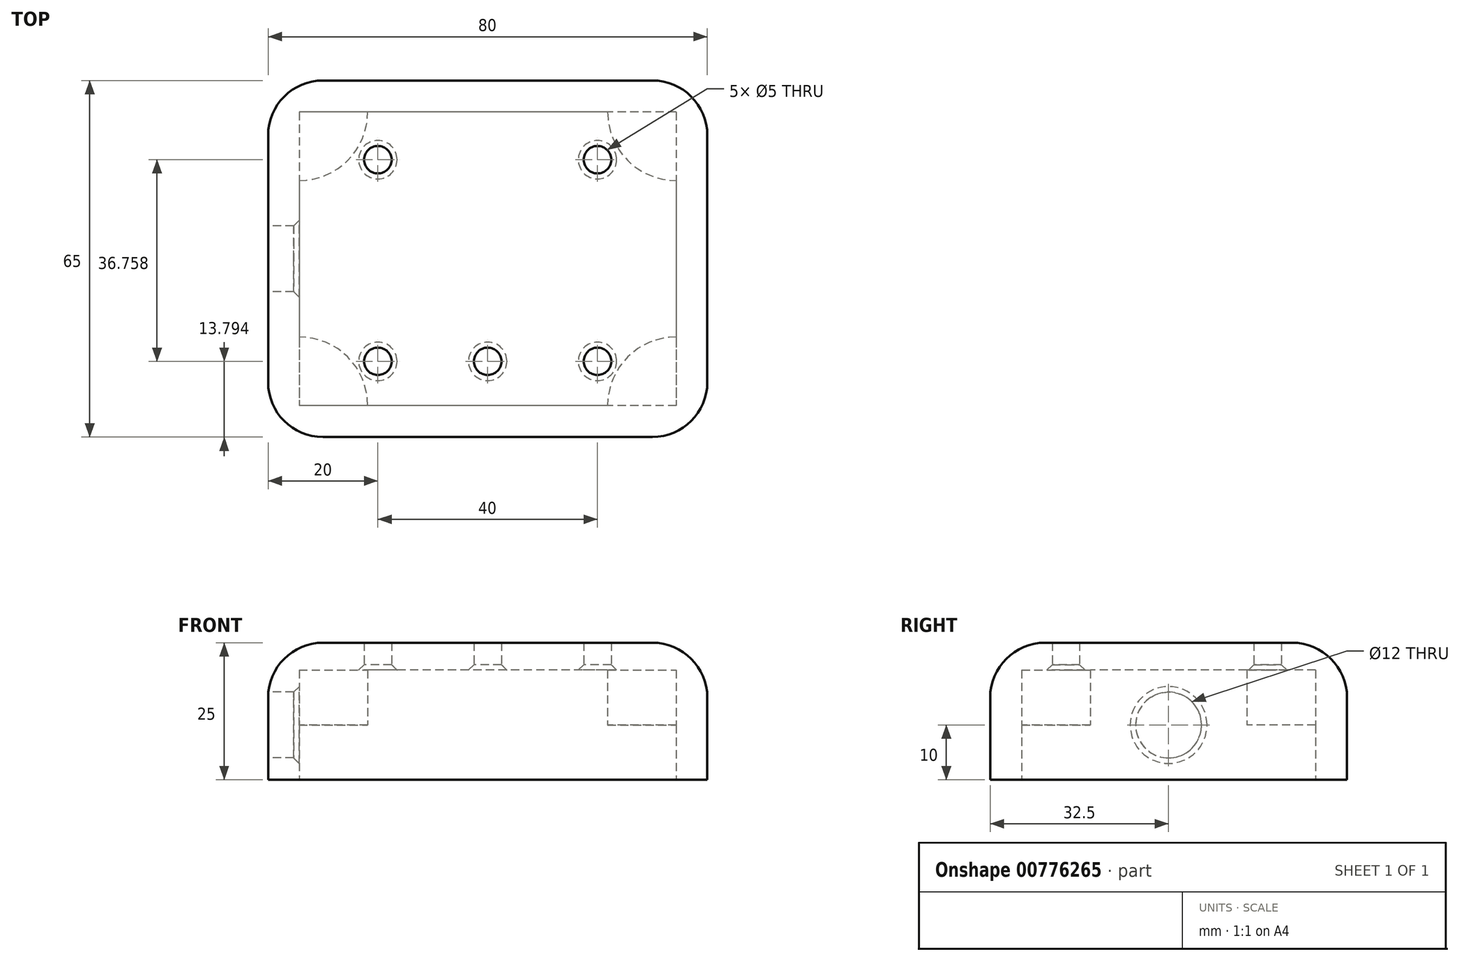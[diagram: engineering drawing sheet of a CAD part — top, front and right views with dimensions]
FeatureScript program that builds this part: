
annotation { "Feature Type Name" : "Feature", "Feature Type Description" : "" }
export const myFeature = defineFeature(function(context is Context, id is Id, definition is map)
    precondition{}
    {
        {
            var Q0;
            Q0=qCreatedBy(makeId("Top.planeOp"),FACE);
            var sketch = newSketch(context, id + "F0", { "sketchPlane" : qUnion([Q0])});
            skLineSegment(sketch, "E0.bottom", {"start": v(40, 32.5) * mm, "end": v(-40, 32.5) * mm});
            skLineSegment(sketch, "E0.top", {"start": v(40, -32.5) * mm, "end": v(-40, -32.5) * mm});
            skLineSegment(sketch, "E0.left", {"start": v(40, 32.5) * mm, "end": v(40, -32.5) * mm});
            skLineSegment(sketch, "E0.right", {"start": v(-40, 32.5) * mm, "end": v(-40, -32.5) * mm});
            skPoint(sketch, "E0.middle", {"position": v(0, 0) * mm});
            skCircle(sketch, "E1", {"center": v(-20, 18.05) * mm, "radius": 2.5 * mm});
            skCircle(sketch, "E2", {"center": v(20, 18.05) * mm, "radius": 2.5 * mm});
            skCircle(sketch, "E3", {"center": v(-20, -18.7) * mm, "radius": 2.5 * mm});
            skCircle(sketch, "E4", {"center": v(0, -18.7) * mm, "radius": 2.5 * mm});
            skCircle(sketch, "E5", {"center": v(20, -18.7) * mm, "radius": 2.5 * mm});
            skSolve(sketch);
        }
        {
            var Q0;
            Q0=qCreatedBy(makeId("Top.planeOp"),FACE);
            var sketch = newSketch(context, id + "F1", { "sketchPlane" : qUnion([Q0])});
            skLineSegment(sketch, "E6.bottom", {"start": v(34.35, 26.75) * mm, "end": v(-34.35, 26.75) * mm});
            skLineSegment(sketch, "E6.top", {"start": v(34.35, -26.75) * mm, "end": v(-34.35, -26.75) * mm});
            skLineSegment(sketch, "E6.left", {"start": v(34.35, 26.75) * mm, "end": v(34.35, -26.75) * mm});
            skLineSegment(sketch, "E6.right", {"start": v(-34.35, 26.75) * mm, "end": v(-34.35, -26.75) * mm});
            skPoint(sketch, "E6.middle", {"position": v(0, 0) * mm});
            skCircle(sketch, "E7", {"center": v(-34.35, 26.75) * mm, "radius": 12.5 * mm});
            skCircle(sketch, "E8", {"center": v(34.35, 26.75) * mm, "radius": 12.5 * mm});
            skCircle(sketch, "E9", {"center": v(34.35, -26.75) * mm, "radius": 12.5 * mm});
            skCircle(sketch, "E10", {"center": v(-34.35, -26.75) * mm, "radius": 12.5 * mm});
            skSolve(sketch);
        }
        {
            var Q0;
            Q0=makeQuery(id+"F0.imprint","IMPRINT",FACE,{"disambiguationData":[TD([[makeQuery(id+"F0.imprint","IMPRINT",EDGE,{"derivedFrom":sQuery(id+"F0.wireOp",EDGE,"E0.bottom")}),1.0]])]});
            extrude(context, id + "F2", {"entities" : qUnion([Q0]), "depth" : 25 * mm, "offsetDistance" : 25 * mm});
        }
        {
            var Q0;
            {var subQ5=sQuery(id+"F1.wireOp",EDGE,"E8");var subQ13=sQuery(id+"F1.wireOp",EDGE,"E6.bottom");var subQ14=makeQuery(id+"F1.imprint","INTERSECT",VERTEX,{"derivedFrom":[subQ13,subQ5]});Q0=makeQuery(id+"F1.imprint","IMPRINT",FACE,{"disambiguationData":[TD([[makeQuery(id+"F1.imprint","IMPRINT",EDGE,{"disambiguationData":[TD([[subQ14,-1.0]])],"derivedFrom":subQ13}),1.0]])]});}
            extrude(context, id + "F3", {"entities" : qUnion([Q0]), "operationType" : NewBodyOperationType.REMOVE, "depth" : 20 * mm, "offsetDistance" : 25 * mm});
        }
        {
            var Q0;
            {var subQ5=sQuery(id+"F1.wireOp",EDGE,"E8");var subQ13=sQuery(id+"F1.wireOp",EDGE,"E6.bottom");var subQ14=makeQuery(id+"F1.imprint","INTERSECT",VERTEX,{"derivedFrom":[subQ13,subQ5]});Q0=makeQuery(id+"F1.imprint","IMPRINT",FACE,{"disambiguationData":[TD([[makeQuery(id+"F1.imprint","IMPRINT",EDGE,{"disambiguationData":[TD([[subQ14,-1.0]])],"derivedFrom":subQ13}),1.0]])]});}
            var Q1;
            {var subQ0=sQuery(id+"F1.wireOp",EDGE,"E6.right");var subQ1=sQuery(id+"F1.wireOp",EDGE,"E6.bottom");var subQ2=makeQuery(id+"F1.imprint","INTERSECT",VERTEX,{"derivedFrom":[subQ1,subQ0]});Q1=makeQuery(id+"F1.imprint","IMPRINT",FACE,{"disambiguationData":[TD([[makeQuery(id+"F1.imprint","IMPRINT",EDGE,{"disambiguationData":[TD([[subQ2,1.0]])],"derivedFrom":subQ1}),1.0]])]});}
            var Q2;
            {var subQ0=sQuery(id+"F1.wireOp",EDGE,"E6.right");var subQ1=sQuery(id+"F1.wireOp",EDGE,"E6.top");var subQ2=makeQuery(id+"F1.imprint","INTERSECT",VERTEX,{"derivedFrom":[subQ1,subQ0]});Q2=makeQuery(id+"F1.imprint","IMPRINT",FACE,{"disambiguationData":[TD([[makeQuery(id+"F1.imprint","IMPRINT",EDGE,{"disambiguationData":[TD([[subQ2,1.0]])],"derivedFrom":subQ1}),-1.0]])]});}
            var Q3;
            {var subQ0=sQuery(id+"F1.wireOp",EDGE,"E6.left");var subQ1=sQuery(id+"F1.wireOp",EDGE,"E6.top");var subQ2=makeQuery(id+"F1.imprint","INTERSECT",VERTEX,{"derivedFrom":[subQ1,subQ0]});Q3=makeQuery(id+"F1.imprint","IMPRINT",FACE,{"disambiguationData":[TD([[makeQuery(id+"F1.imprint","IMPRINT",EDGE,{"disambiguationData":[TD([[subQ2,-1.0]])],"derivedFrom":subQ1}),-1.0]])]});}
            var Q4;
            {var subQ0=sQuery(id+"F1.wireOp",EDGE,"E6.left");var subQ1=sQuery(id+"F1.wireOp",EDGE,"E6.bottom");var subQ2=makeQuery(id+"F1.imprint","INTERSECT",VERTEX,{"derivedFrom":[subQ1,subQ0]});Q4=makeQuery(id+"F1.imprint","IMPRINT",FACE,{"disambiguationData":[TD([[makeQuery(id+"F1.imprint","IMPRINT",EDGE,{"disambiguationData":[TD([[subQ2,-1.0]])],"derivedFrom":subQ1}),1.0]])]});}
            extrude(context, id + "F4", {"entities" : qUnion([Q0, Q1, Q2, Q3, Q4]), "operationType" : NewBodyOperationType.REMOVE, "depth" : 10 * mm, "offsetDistance" : 25 * mm});
        }
        {
            var Q0;
            Q0=makeQuery(id+"F2.opExtrude","CAP_EDGE",EDGE,{"disambiguationData":[OSD([sQuery(id+"F0.wireOp",EDGE,"E0.bottom")])],"isStart":false});
            var Q1;
            Q1=makeQuery(id+"F2.opExtrude","CAP_EDGE",EDGE,{"disambiguationData":[OSD([sQuery(id+"F0.wireOp",EDGE,"E0.left")])],"isStart":false});
            var Q2;
            Q2=makeQuery(id+"F2.opExtrude","CAP_EDGE",EDGE,{"disambiguationData":[OSD([sQuery(id+"F0.wireOp",EDGE,"E0.top")])],"isStart":false});
            var Q3;
            Q3=makeQuery(id+"F2.opExtrude","CAP_EDGE",EDGE,{"disambiguationData":[OSD([sQuery(id+"F0.wireOp",EDGE,"E0.right")])],"isStart":false});
            var Q4;
            Q4=makeQuery(id+"F2.opExtrude","SWEPT_EDGE",EDGE,{"disambiguationData":[OSD([sQuery(id+"F0.wireOp",EDGE,"E0.top"),sQuery(id+"F0.wireOp",EDGE,"E0.right")])]});
            var Q5;
            Q5=makeQuery(id+"F2.opExtrude","SWEPT_EDGE",EDGE,{"disambiguationData":[OSD([sQuery(id+"F0.wireOp",EDGE,"E0.bottom"),sQuery(id+"F0.wireOp",EDGE,"E0.right")])]});
            var Q6;
            Q6=makeQuery(id+"F2.opExtrude","SWEPT_EDGE",EDGE,{"disambiguationData":[OSD([sQuery(id+"F0.wireOp",EDGE,"E0.bottom"),sQuery(id+"F0.wireOp",EDGE,"E0.left")])]});
            var Q7;
            Q7=makeQuery(id+"F2.opExtrude","SWEPT_EDGE",EDGE,{"disambiguationData":[OSD([sQuery(id+"F0.wireOp",EDGE,"E0.top"),sQuery(id+"F0.wireOp",EDGE,"E0.left")])]});
            fillet(context, id + "F5", {"entities" : qUnion([Q0, Q1, Q2, Q3, Q4, Q5, Q6, Q7]), "radius" : 10 * mm, "tangentPropagation" : true, "allowEdgeOverflow" : false});
        }
        {
            var Q0;
            Q0=makeQuery(id+"F2.opExtrude","SWEPT_FACE",FACE,{"disambiguationData":[OSD([sQuery(id+"F0.wireOp",EDGE,"E0.right")])]});
            var sketch = newSketch(context, id + "F6", { "sketchPlane" : qUnion([Q0])});
            skCircle(sketch, "E11", {"center": v(0, 10) * mm, "radius": 6 * mm});
            skSolve(sketch);
        }
        {
            var Q0;
            {var subQ0=sQuery(id+"F6.wireOp",EDGE,"E11");var subQ1=sQuery(id+"F0.wireOp",EDGE,"E0.right");var subQ2=makeQuery(id+"F5.opFillet","BLEND_EDGE",EDGE,{"blendedFrom":[makeQuery(id+"F2.opExtrude","CAP_EDGE",EDGE,{"disambiguationData":[OSD([subQ1])],"isStart":false}),makeQuery(id+"F2.opExtrude","SWEPT_FACE",FACE,{"disambiguationData":[OSD([subQ1])]})],"blendedInto":[makeQuery(id+"F2.opExtrude","SWEPT_FACE",FACE,{"disambiguationData":[OSD([subQ1])]})]});var subQ3=makeQuery(id+"F6.imprint","INTERSECT",VERTEX,{"disambiguationData":[OD(0.0)],"derivedFrom":[subQ2,subQ0]});Q0=makeQuery(id+"F6.imprint","IMPRINT",FACE,{"disambiguationData":[TD([[makeQuery(id+"F6.imprint","IMPRINT",EDGE,{"disambiguationData":[TD([[subQ3,-1.0]])],"derivedFrom":subQ0}),1.0]])]});}
            var Q1;
            {var subQ0=sQuery(id+"F6.wireOp",EDGE,"E11");var subQ1=sQuery(id+"F0.wireOp",EDGE,"E0.right");var subQ2=makeQuery(id+"F5.opFillet","BLEND_EDGE",EDGE,{"blendedFrom":[makeQuery(id+"F2.opExtrude","CAP_EDGE",EDGE,{"disambiguationData":[OSD([subQ1])],"isStart":false}),makeQuery(id+"F2.opExtrude","SWEPT_FACE",FACE,{"disambiguationData":[OSD([subQ1])]})],"blendedInto":[makeQuery(id+"F2.opExtrude","SWEPT_FACE",FACE,{"disambiguationData":[OSD([subQ1])]})]});var subQ3=makeQuery(id+"F6.imprint","INTERSECT",VERTEX,{"disambiguationData":[OD(0.0)],"derivedFrom":[subQ2,subQ0]});Q1=makeQuery(id+"F6.imprint","IMPRINT",FACE,{"disambiguationData":[TD([[makeQuery(id+"F6.imprint","IMPRINT",EDGE,{"disambiguationData":[TD([[subQ3,1.0]])],"derivedFrom":subQ0}),1.0]])]});}
            extrude(context, id + "F7", {"entities" : qUnion([Q0, Q1]), "operationType" : NewBodyOperationType.REMOVE, "oppositeDirection" : true, "depth" : 10 * mm, "offsetDistance" : 25 * mm});
        }
        {
            var Q0;
            Q0=makeQuery(id+"F3.boolean.opBoolean","INTERSECT",EDGE,{"derivedFrom":[makeQuery(id+"F2.opExtrude","SWEPT_FACE",FACE,{"disambiguationData":[OSD([sQuery(id+"F0.wireOp",EDGE,"E1")])]}),makeQuery(id+"F3.opExtrude","CAP_FACE",FACE,{"disambiguationData":[OSD([sQuery(id+"F1.wireOp",EDGE,"E6.bottom"),sQuery(id+"F1.wireOp",EDGE,"E6.top"),sQuery(id+"F1.wireOp",EDGE,"E6.left"),sQuery(id+"F1.wireOp",EDGE,"E6.right"),sQuery(id+"F1.wireOp",EDGE,"E7"),sQuery(id+"F1.wireOp",EDGE,"E8"),sQuery(id+"F1.wireOp",EDGE,"E9"),sQuery(id+"F1.wireOp",EDGE,"E10")])],"isStart":false})]});
            var Q1;
            Q1=makeQuery(id+"F3.boolean.opBoolean","INTERSECT",EDGE,{"derivedFrom":[makeQuery(id+"F2.opExtrude","SWEPT_FACE",FACE,{"disambiguationData":[OSD([sQuery(id+"F0.wireOp",EDGE,"E3")])]}),makeQuery(id+"F3.opExtrude","CAP_FACE",FACE,{"disambiguationData":[OSD([sQuery(id+"F1.wireOp",EDGE,"E6.bottom"),sQuery(id+"F1.wireOp",EDGE,"E6.top"),sQuery(id+"F1.wireOp",EDGE,"E6.left"),sQuery(id+"F1.wireOp",EDGE,"E6.right"),sQuery(id+"F1.wireOp",EDGE,"E7"),sQuery(id+"F1.wireOp",EDGE,"E8"),sQuery(id+"F1.wireOp",EDGE,"E9"),sQuery(id+"F1.wireOp",EDGE,"E10")])],"isStart":false})]});
            var Q2;
            Q2=makeQuery(id+"F3.boolean.opBoolean","INTERSECT",EDGE,{"derivedFrom":[makeQuery(id+"F2.opExtrude","SWEPT_FACE",FACE,{"disambiguationData":[OSD([sQuery(id+"F0.wireOp",EDGE,"E4")])]}),makeQuery(id+"F3.opExtrude","CAP_FACE",FACE,{"disambiguationData":[OSD([sQuery(id+"F1.wireOp",EDGE,"E6.bottom"),sQuery(id+"F1.wireOp",EDGE,"E6.top"),sQuery(id+"F1.wireOp",EDGE,"E6.left"),sQuery(id+"F1.wireOp",EDGE,"E6.right"),sQuery(id+"F1.wireOp",EDGE,"E7"),sQuery(id+"F1.wireOp",EDGE,"E8"),sQuery(id+"F1.wireOp",EDGE,"E9"),sQuery(id+"F1.wireOp",EDGE,"E10")])],"isStart":false})]});
            var Q3;
            Q3=makeQuery(id+"F3.boolean.opBoolean","INTERSECT",EDGE,{"derivedFrom":[makeQuery(id+"F2.opExtrude","SWEPT_FACE",FACE,{"disambiguationData":[OSD([sQuery(id+"F0.wireOp",EDGE,"E5")])]}),makeQuery(id+"F3.opExtrude","CAP_FACE",FACE,{"disambiguationData":[OSD([sQuery(id+"F1.wireOp",EDGE,"E6.bottom"),sQuery(id+"F1.wireOp",EDGE,"E6.top"),sQuery(id+"F1.wireOp",EDGE,"E6.left"),sQuery(id+"F1.wireOp",EDGE,"E6.right"),sQuery(id+"F1.wireOp",EDGE,"E7"),sQuery(id+"F1.wireOp",EDGE,"E8"),sQuery(id+"F1.wireOp",EDGE,"E9"),sQuery(id+"F1.wireOp",EDGE,"E10")])],"isStart":false})]});
            var Q4;
            Q4=makeQuery(id+"F3.boolean.opBoolean","INTERSECT",EDGE,{"derivedFrom":[makeQuery(id+"F2.opExtrude","SWEPT_FACE",FACE,{"disambiguationData":[OSD([sQuery(id+"F0.wireOp",EDGE,"E2")])]}),makeQuery(id+"F3.opExtrude","CAP_FACE",FACE,{"disambiguationData":[OSD([sQuery(id+"F1.wireOp",EDGE,"E6.bottom"),sQuery(id+"F1.wireOp",EDGE,"E6.top"),sQuery(id+"F1.wireOp",EDGE,"E6.left"),sQuery(id+"F1.wireOp",EDGE,"E6.right"),sQuery(id+"F1.wireOp",EDGE,"E7"),sQuery(id+"F1.wireOp",EDGE,"E8"),sQuery(id+"F1.wireOp",EDGE,"E9"),sQuery(id+"F1.wireOp",EDGE,"E10")])],"isStart":false})]});
            var Q5;
            {var subQ0=sQuery(id+"F1.wireOp",EDGE,"E6.right");Q5=makeQuery(id+"F7.boolean.opBoolean","INTERSECT",EDGE,{"derivedFrom":[makeQuery(id+"F4.boolean.opBoolean","MERGE",FACE,{"derivedFrom":[makeQuery(id+"F3.boolean.opBoolean","COPY",FACE,{"derivedFrom":makeQuery(id+"F3.opExtrude","SWEPT_FACE",FACE,{"disambiguationData":[OSD([subQ0])]})}),makeQuery(id+"F4.opExtrude","SWEPT_FACE",FACE,{"disambiguationData":[OSD([subQ0])]})]}),makeQuery(id+"F7.opExtrude","SWEPT_FACE",FACE,{"disambiguationData":[OSD([sQuery(id+"F6.wireOp",EDGE,"E11")])]})]});}
            chamfer(context, id + "F8", {"entities" : qUnion([Q0, Q1, Q2, Q3, Q4, Q5]), "width" : 1 * mm, "tangentPropagation" : true});
        }
    });
